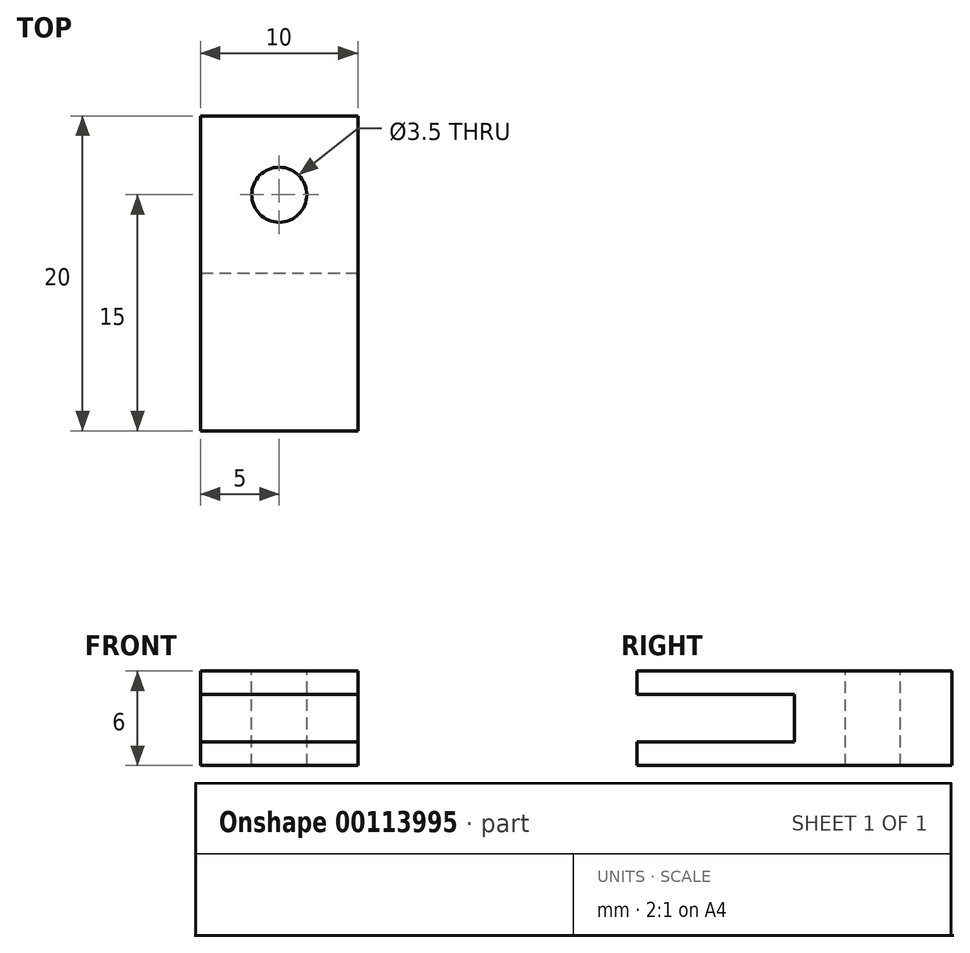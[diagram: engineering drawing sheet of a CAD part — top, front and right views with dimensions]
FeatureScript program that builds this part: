
annotation { "Feature Type Name" : "Feature", "Feature Type Description" : "" }
export const myFeature = defineFeature(function(context is Context, id is Id, definition is map)
    precondition{}
    {
        {
            var Q0;
            Q0=qCreatedBy(makeId("Right.planeOp"),FACE);
            var sketch = newSketch(context, id + "F0", { "sketchPlane" : qUnion([Q0])});
            skLineSegment(sketch, "E0.bottom", {"start": v(10, -3.07) * mm, "end": v(-10, -3.07) * mm});
            skLineSegment(sketch, "E0.top", {"start": v(10, 2.93) * mm, "end": v(-10, 2.93) * mm});
            skLineSegment(sketch, "E0.left", {"start": v(10, -3.07) * mm, "end": v(10, 2.93) * mm});
            skLineSegment(sketch, "E0.right", {"start": v(-10, -3.07) * mm, "end": v(-10, 2.93) * mm});
            skPoint(sketch, "E0.middle", {"position": v(0, -0.07) * mm});
            skLineSegment(sketch, "E1.bottom", {"start": v(-10, 1.43) * mm, "end": v(0, 1.43) * mm});
            skLineSegment(sketch, "E1.top", {"start": v(-10, -1.57) * mm, "end": v(0, -1.57) * mm});
            skLineSegment(sketch, "E1.left", {"start": v(-10, 1.43) * mm, "end": v(-10, -1.57) * mm});
            skLineSegment(sketch, "E1.right", {"start": v(0, 1.43) * mm, "end": v(0, -1.57) * mm});
            skSolve(sketch);
        }
        {
            var Q0;
            {var subQ1=sQuery(id+"F0.wireOp",EDGE,"E0.bottom");Q0=makeQuery(id+"F0.imprint","IMPRINT",FACE,{"disambiguationData":[TD([[makeQuery(id+"F0.imprint","IMPRINT",EDGE,{"derivedFrom":subQ1}),-1.0]])]});}
            extrude(context, id + "F1", {"entities" : qUnion([Q0]), "depth" : 10 * mm});
        }
        {
            var Q0;
            Q0=makeQuery(id+"F1.opExtrude","SWEPT_FACE",FACE,{"disambiguationData":[OSD([sQuery(id+"F0.wireOp",EDGE,"E0.top")])]});
            var sketch = newSketch(context, id + "F2", { "sketchPlane" : qUnion([Q0])});
            skLineSegment(sketch, "E2", {"start": v(10, 10) * mm, "end": v(0, 0) * mm});
            skCircle(sketch, "E3", {"center": v(5, 5) * mm, "radius": 2.08 * mm});
            skSolve(sketch);
        }
        {
            var Q0;
            Q0=sQuery(id+"F2.wireOp",VERTEX,"E3.center");
            var Q1;
            Q1=makeQuery(id+"F1.opExtrude","SWEPT_BODY",BODY,{"disambiguationData":[OSD([sQuery(id+"F0.wireOp",EDGE,"E0.bottom"),sQuery(id+"F0.wireOp",EDGE,"E0.top"),sQuery(id+"F0.wireOp",EDGE,"E0.left"),sQuery(id+"F0.wireOp",EDGE,"E0.right"),sQuery(id+"F0.wireOp",EDGE,"E1.bottom"),sQuery(id+"F0.wireOp",EDGE,"E1.top"),sQuery(id+"F0.wireOp",EDGE,"E1.right")])]});
            hole(context, id + "F3", {"style" : HoleStyle.SIMPLE, "endStyle" : HoleEndStyle.THROUGH, "holeDiameter" : 3.5 * mm, "locations" : qUnion([Q0]), "scope" : qUnion([Q1]), "isTappedThrough" : true});
        }
    });
